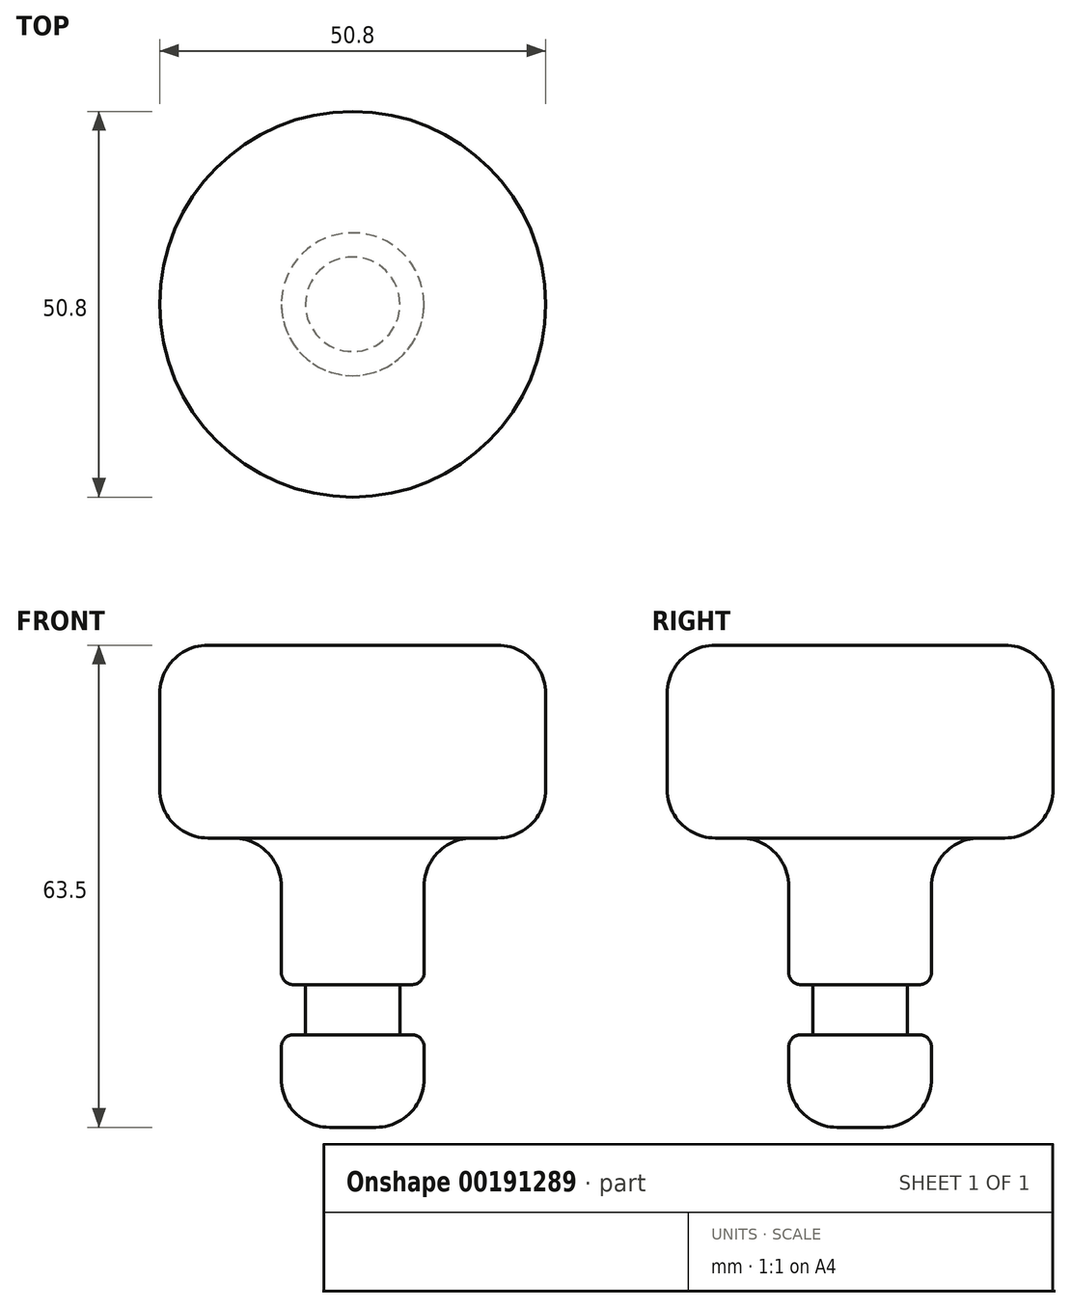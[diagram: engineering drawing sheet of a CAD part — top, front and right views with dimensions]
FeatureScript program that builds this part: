
annotation { "Feature Type Name" : "Feature", "Feature Type Description" : "" }
export const myFeature = defineFeature(function(context is Context, id is Id, definition is map)
    precondition{}
    {
        {
            var Q0;
            Q0=qCreatedBy(makeId("Front.planeOp"),FACE);
            var sketch = newSketch(context, id + "F0", { "sketchPlane" : qUnion([Q0])});
            skLineSegment(sketch, "E0", {"start": v(0, 25.4) * mm, "end": v(25.4, 25.4) * mm});
            skLineSegment(sketch, "E1", {"start": v(25.4, 25.4) * mm, "end": v(25.4, 0) * mm});
            skLineSegment(sketch, "E2", {"start": v(25.4, 0) * mm, "end": v(9.4, 0) * mm});
            skLineSegment(sketch, "E3", {"start": v(9.4, 0) * mm, "end": v(9.4, -19.3) * mm});
            skLineSegment(sketch, "E4", {"start": v(9.4, -38.1) * mm, "end": v(0, -38.1) * mm});
            skLineSegment(sketch, "E5", {"start": v(0, 57.89) * mm, "end": v(0, -56.9) * mm, "construction": true});
            skLineSegment(sketch, "E6", {"start": v(0, 25.4) * mm, "end": v(0, -38.1) * mm});
            skPoint(sketch, "E7.endSnap0", {"position": v(4.7, -38.1) * mm});
            skLineSegment(sketch, "E8", {"start": v(6.22, -25.9) * mm, "end": v(9.4, -25.9) * mm});
            skLineSegment(sketch, "E9.trimOffspring", {"start": v(9.4, -25.9) * mm, "end": v(9.4, -38.1) * mm});
            skLineSegment(sketch, "E10", {"start": v(6.22, -25.9) * mm, "end": v(6.22, -19.3) * mm});
            skLineSegment(sketch, "E11", {"start": v(6.22, -19.3) * mm, "end": v(9.4, -19.3) * mm});
            skPoint(sketch, "E12.orphan", {"position": v(3.05, -25.9) * mm});
            skSolve(sketch);
        }
        {
            var Q0;
            Q0 = qSketchRegion(id + "F0", true);
            var Q1;
            Q1=sQuery(id+"F0.wireOp",EDGE,"E5");
            revolve(context, id + "F1", {"entities" : qUnion([Q0]), "axis" : qUnion([Q1]), "revolveType" : RevolveType.FULL});
        }
        {
            var Q0;
            Q0=makeQuery(id+"F1.opRevolve","SWEPT_FACE",FACE,{"disambiguationData":[OSD([sQuery(id+"F0.wireOp",EDGE,"E1")])]});
            var Q1;
            Q1=makeQuery(id+"F1.opRevolve","SWEPT_EDGE",EDGE,{"disambiguationData":[OSD([sQuery(id+"F0.wireOp",EDGE,"E4"),sQuery(id+"F0.wireOp",EDGE,"E9.trimOffspring")])]});
            var Q2;
            Q2=makeQuery(id+"F1.opRevolve","SWEPT_EDGE",EDGE,{"disambiguationData":[OSD([sQuery(id+"F0.wireOp",EDGE,"E2"),sQuery(id+"F0.wireOp",EDGE,"E3")])]});
            fillet(context, id + "F2", {"entities" : qUnion([Q0, Q1, Q2]), "radius" : 6.35 * mm, "tangentPropagation" : true, "allowEdgeOverflow" : false});
        }
        {
            var Q0;
            Q0=makeQuery(id+"F1.opRevolve","SWEPT_EDGE",EDGE,{"disambiguationData":[OSD([sQuery(id+"F0.wireOp",EDGE,"E3"),sQuery(id+"F0.wireOp",EDGE,"E11")])]});
            var Q1;
            Q1=makeQuery(id+"F1.opRevolve","SWEPT_EDGE",EDGE,{"disambiguationData":[OSD([sQuery(id+"F0.wireOp",EDGE,"E8"),sQuery(id+"F0.wireOp",EDGE,"E9.trimOffspring")])]});
            fillet(context, id + "F3", {"entities" : qUnion([Q0, Q1]), "radius" : 1.59 * mm, "tangentPropagation" : true, "allowEdgeOverflow" : false});
        }
    });
